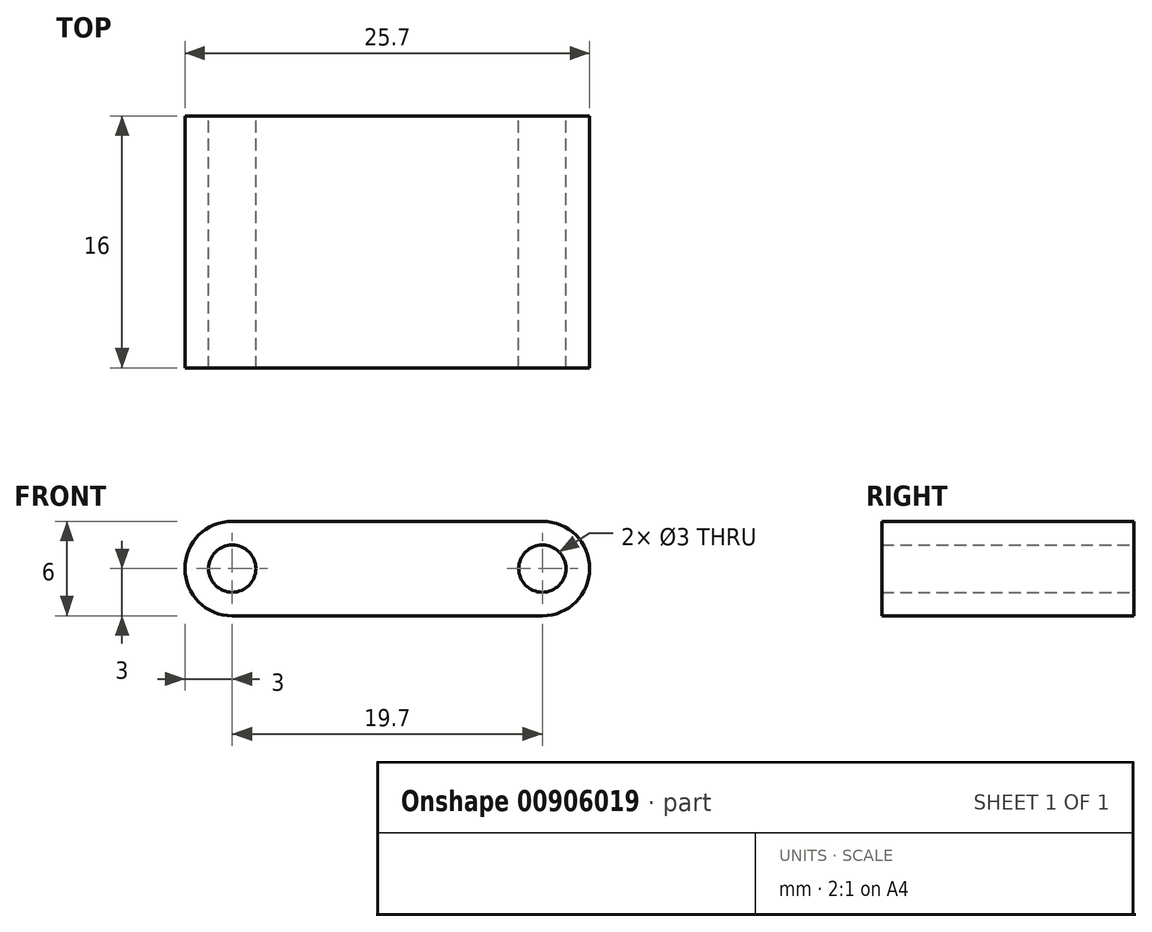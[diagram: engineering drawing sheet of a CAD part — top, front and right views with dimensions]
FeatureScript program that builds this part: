
annotation { "Feature Type Name" : "Feature", "Feature Type Description" : "" }
export const myFeature = defineFeature(function(context is Context, id is Id, definition is map)
    precondition{}
    {
        {
            var Q0;
            Q0=qCreatedBy(makeId("Front.planeOp"),FACE);
            var sketch = newSketch(context, id + "F0", { "sketchPlane" : qUnion([Q0])});
            skLineSegment(sketch, "E0", {"start": v(-9.85, 0) * mm, "end": v(9.85, 0) * mm});
            skCircle(sketch, "E1", {"center": v(9.85, 0) * mm, "radius": 1.5 * mm});
            skCircle(sketch, "E2", {"center": v(-9.85, 0) * mm, "radius": 1.5 * mm});
            skPoint(sketch, "E3.visualSharp", {"position": v(-66.12, -69.63) * mm});
            skArc(sketch, "E3.filletArc", {"start": v(-51.94, -37.1) * mm, "mid": v(-52.74, -38.3) * mm, "end": v(-51.92, -39.49) * mm});
            skArc(sketch, "E4", {"start": v(-9.85, 3) * mm, "mid": v(-12.85, 0) * mm, "end": v(-9.85, -3) * mm});
            skArc(sketch, "E5", {"start": v(9.85, -3) * mm, "mid": v(12.85, 0) * mm, "end": v(9.85, 3) * mm});
            skLineSegment(sketch, "E6", {"start": v(9.85, 3) * mm, "end": v(-9.85, 3) * mm});
            skLineSegment(sketch, "E7", {"start": v(-9.85, -3) * mm, "end": v(9.85, -3) * mm});
            skSolve(sketch);
        }
        {
            var Q0;
            Q0=qSketchRegion(id+"F0",true);
            extrude(context, id + "F1", {"entities" : qUnion([Q0]), "endBound" : BoundingType.SYMMETRIC, "depth" : 16 * mm, "offsetDistance" : 25.4 * mm});
        }
    });
